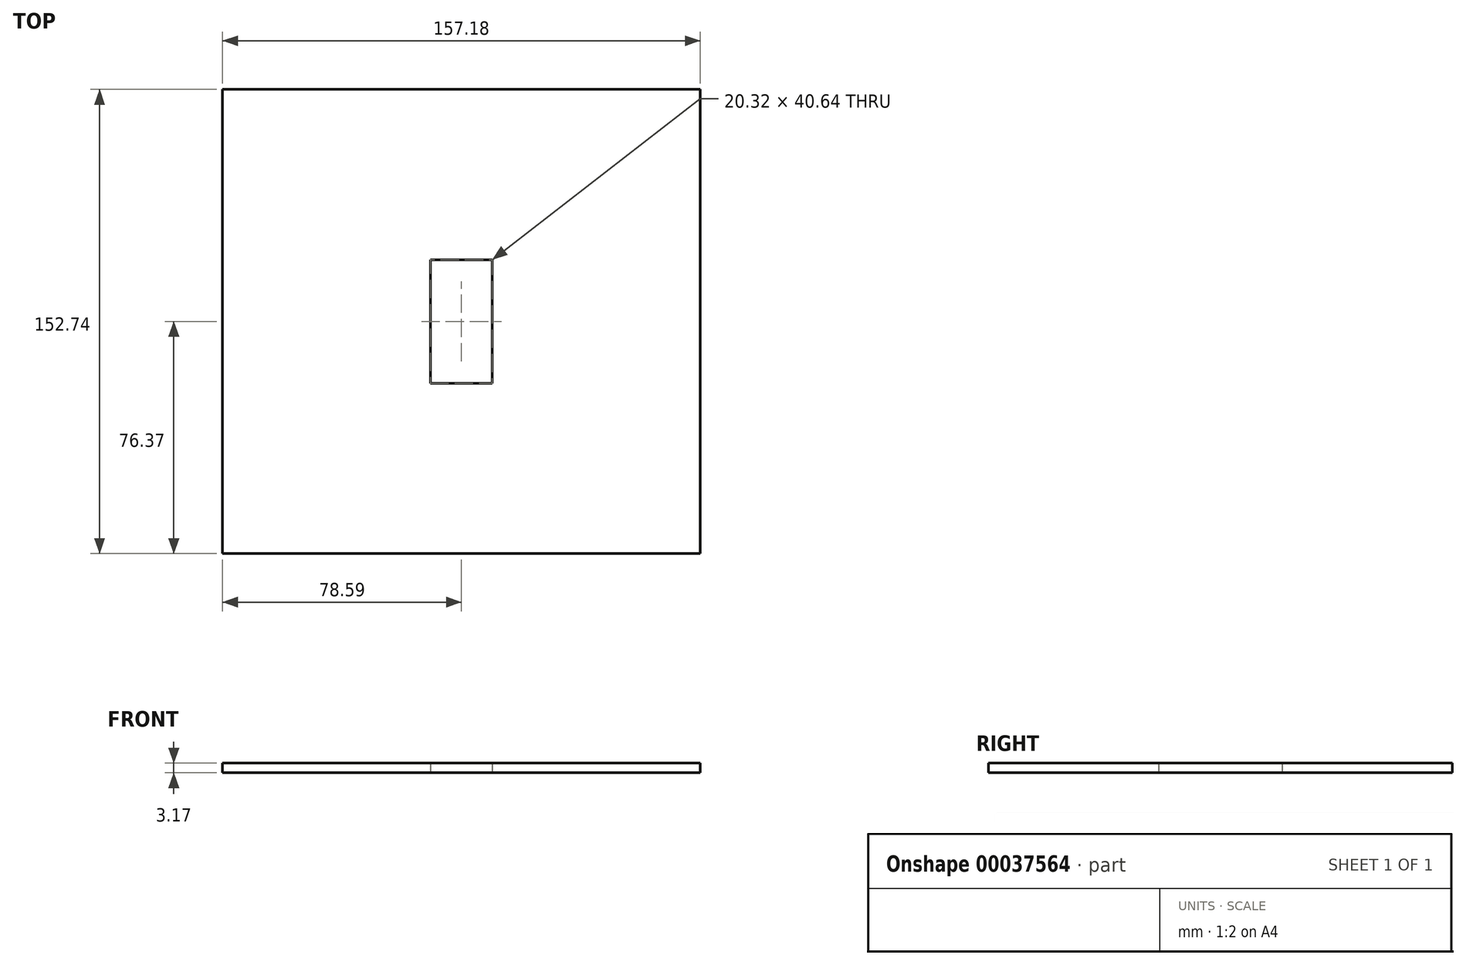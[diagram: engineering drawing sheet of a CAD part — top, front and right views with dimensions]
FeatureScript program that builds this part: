
annotation { "Feature Type Name" : "Feature", "Feature Type Description" : "" }
export const myFeature = defineFeature(function(context is Context, id is Id, definition is map)
    precondition{}
    {
        {
            var Q0;
            Q0=qCreatedBy(makeId("Top.planeOp"),FACE);
            var sketch = newSketch(context, id + "F0", { "sketchPlane" : qUnion([Q0])});
            skLineSegment(sketch, "E0.rect.bottom", {"start": v(78.6, -76.37) * mm, "end": v(-78.6, -76.37) * mm});
            skLineSegment(sketch, "E0.rect.top", {"start": v(78.6, 76.37) * mm, "end": v(-78.6, 76.37) * mm});
            skLineSegment(sketch, "E0.rect.left", {"start": v(78.6, -76.37) * mm, "end": v(78.6, 76.37) * mm});
            skLineSegment(sketch, "E0.rect.right", {"start": v(-78.6, -76.37) * mm, "end": v(-78.6, 76.37) * mm});
            skPoint(sketch, "E0.rect.middle", {"position": v(0, 0) * mm});
            skLineSegment(sketch, "E1.rect.bottom", {"start": v(10.16, -20.32) * mm, "end": v(-10.16, -20.32) * mm});
            skLineSegment(sketch, "E1.rect.top", {"start": v(10.16, 20.32) * mm, "end": v(-10.16, 20.32) * mm});
            skLineSegment(sketch, "E1.rect.left", {"start": v(10.16, -20.32) * mm, "end": v(10.16, 20.32) * mm});
            skLineSegment(sketch, "E1.rect.right", {"start": v(-10.16, -20.32) * mm, "end": v(-10.16, 20.32) * mm});
            skSolve(sketch);
        }
        {
            var Q0;
            Q0=makeQuery(id+"F0.imprint","IMPRINT",FACE,{"disambiguationData":[TD([[makeQuery(id+"F0.imprint","IMPRINT",EDGE,{"derivedFrom":sQuery(id+"F0.wireOp",EDGE,"E0.rect.bottom")}),-1.0]])]});
            extrude(context, id + "F1", {"entities" : qUnion([Q0]), "depth" : 3.17 * mm});
        }
    });
